# Revit family: RVT_MACON_MN7xC-x 03 23 A
name_source: partatom
category: Specialty Equipment
units: mm (PartAtom-declared; Revit-internal decimal feet)

## family parameters
Always vertical = Yes
Cut with Voids When Loaded = No
OmniClass Number = 23.40.40.14.17
OmniClass Title = Food Cooking Equipment
Part Type = Normal
Room Calculation Point = No
Round Connector Dimension = Use Diameter
Shared = No
Work Plane-Based = No

## types (4) — shared parameters
Default Elevation = 0 mm
Depth = 972 mm
Height = 245 mm
Manufacturer = MACOM
URL = https://www.acosmacom.com.br

## per-type parameters (varying)
| type | Description | Door 1 | Door 2 | Model | Show Clearances | Volume | Weight | Width |
| MN92C-G | MÓDULO NEUTRO COM GAVETA 720 MACOM | Yes | Yes | MN72C-G | Yes | 1,3 m³ | 20,00 kg | 900 mm |
| MN91C-G | MÓDULO NEUTRO COM GAVETA 360 MACOM | Yes | Yes | MN71C-G | Yes | 0,06 m³ | 13,00 kg | 450 mm |
| MN92C-S | MÓDULO NEUTRO SIMPLES 720 MACOM | No | No | MN72C-S | No | 1,3 m³ | 20,00 kg | 900 mm |
| MN91C-S | MÓDULO NEUTRO SIMPLES 360 MACOM | No | No | MN71C-S | No | 0,06 m³ | 13,00 kg | 450 mm |
